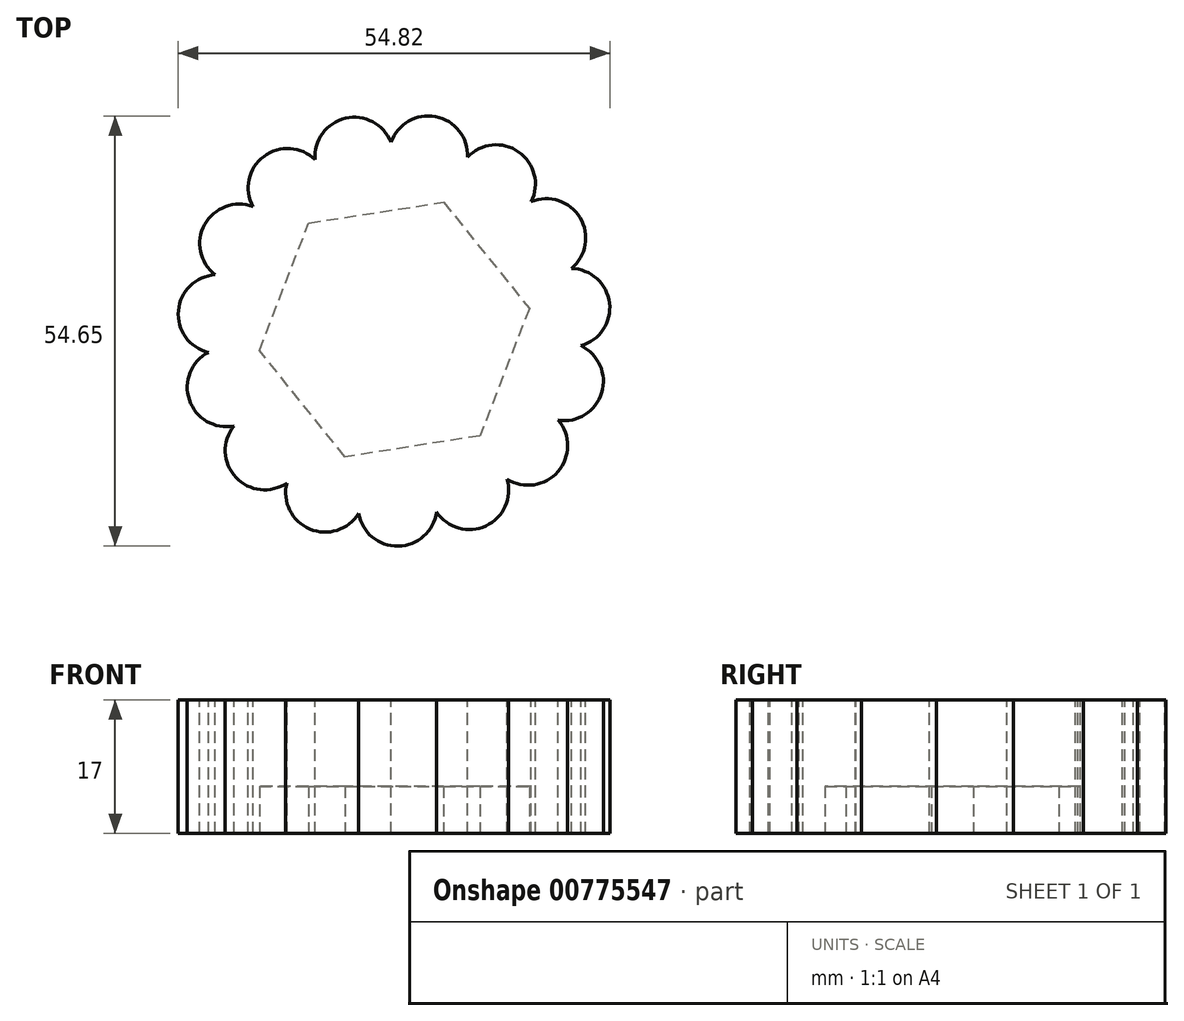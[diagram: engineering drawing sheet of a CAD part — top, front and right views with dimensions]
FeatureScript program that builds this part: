
annotation { "Feature Type Name" : "Feature", "Feature Type Description" : "" }
export const myFeature = defineFeature(function(context is Context, id is Id, definition is map)
    precondition{}
    {
        {
            var Q0;
            Q0=qCreatedBy(makeId("Top.planeOp"),FACE);
            var sketch = newSketch(context, id + "F0", { "sketchPlane" : qUnion([Q0])});
            skCircle(sketch, "E0.cCircle", {"center": v(0, 0) * mm, "radius": 17.35 * mm, "construction": true});
            skLineSegment(sketch, "E0.0", {"start": v(10.88, -13.52) * mm, "end": v(-6.27, -16.18) * mm});
            skLineSegment(sketch, "E0.1", {"start": v(-6.27, -16.18) * mm, "end": v(-17.14, -2.66) * mm});
            skLineSegment(sketch, "E0.2", {"start": v(-17.14, -2.66) * mm, "end": v(-10.88, 13.52) * mm});
            skLineSegment(sketch, "E0.3", {"start": v(-10.88, 13.52) * mm, "end": v(6.27, 16.18) * mm});
            skLineSegment(sketch, "E0.4", {"start": v(6.27, 16.18) * mm, "end": v(17.14, 2.66) * mm});
            skLineSegment(sketch, "E0.5", {"start": v(17.14, 2.66) * mm, "end": v(10.88, -13.52) * mm});
            skCircle(sketch, "E1.cCircle", {"center": v(0, 0) * mm, "radius": 22.54 * mm, "construction": true});
            skLineSegment(sketch, "E1.0", {"start": v(15.15, -16.68) * mm, "end": v(-6.87, -21.46) * mm});
            skLineSegment(sketch, "E1.1", {"start": v(-6.87, -21.46) * mm, "end": v(-22.02, -4.78) * mm});
            skLineSegment(sketch, "E1.2", {"start": v(-22.02, -4.78) * mm, "end": v(-15.15, 16.68) * mm});
            skLineSegment(sketch, "E1.3", {"start": v(-15.15, 16.68) * mm, "end": v(6.87, 21.46) * mm});
            skLineSegment(sketch, "E1.4", {"start": v(6.87, 21.46) * mm, "end": v(22.02, 4.78) * mm});
            skLineSegment(sketch, "E1.5", {"start": v(22.02, 4.78) * mm, "end": v(15.15, -16.68) * mm});
            skSolve(sketch);
        }
        {
            var Q0;
            Q0 = qSketchRegion(id + "F0", true);
            extrude(context, id + "F1", {"entities" : qUnion([Q0]), "depth" : 12 * mm, "offsetDistance" : 25 * mm});
        }
        {
            var Q0;
            Q0=makeQuery(id+"F1.opExtrude","CAP_FACE",FACE,{"disambiguationData":[OSD([sQuery(id+"F0.wireOp",EDGE,"E0.0"),sQuery(id+"F0.wireOp",EDGE,"E0.1"),sQuery(id+"F0.wireOp",EDGE,"E0.2"),sQuery(id+"F0.wireOp",EDGE,"E0.3"),sQuery(id+"F0.wireOp",EDGE,"E0.4"),sQuery(id+"F0.wireOp",EDGE,"E0.5"),sQuery(id+"F0.wireOp",EDGE,"E1.0"),sQuery(id+"F0.wireOp",EDGE,"E1.1"),sQuery(id+"F0.wireOp",EDGE,"E1.2"),sQuery(id+"F0.wireOp",EDGE,"E1.3"),sQuery(id+"F0.wireOp",EDGE,"E1.4"),sQuery(id+"F0.wireOp",EDGE,"E1.5")])],"isStart":false});
            extrude(context, id + "F2", {"entities" : qUnion([Q0]), "operationType" : NewBodyOperationType.ADD, "oppositeDirection" : true, "depth" : 6 * mm, "offsetDistance" : 25 * mm});
        }
        {
            var Q0;
            Q0=makeQuery(id+"F1.opExtrude","CAP_FACE",FACE,{"disambiguationData":[OSD([sQuery(id+"F0.wireOp",EDGE,"E0.0"),sQuery(id+"F0.wireOp",EDGE,"E0.1"),sQuery(id+"F0.wireOp",EDGE,"E0.2"),sQuery(id+"F0.wireOp",EDGE,"E0.3"),sQuery(id+"F0.wireOp",EDGE,"E0.4"),sQuery(id+"F0.wireOp",EDGE,"E0.5"),sQuery(id+"F0.wireOp",EDGE,"E1.0"),sQuery(id+"F0.wireOp",EDGE,"E1.1"),sQuery(id+"F0.wireOp",EDGE,"E1.2"),sQuery(id+"F0.wireOp",EDGE,"E1.3"),sQuery(id+"F0.wireOp",EDGE,"E1.4"),sQuery(id+"F0.wireOp",EDGE,"E1.5")])],"isStart":false});
            var sketch = newSketch(context, id + "F3", { "sketchPlane" : qUnion([Q0])});
            skCircle(sketch, "E2.cCircle", {"center": v(0, 0) * mm, "radius": 22.54 * mm, "construction": true});
            skLineSegment(sketch, "E2.0", {"start": v(15.15, -16.68) * mm, "end": v(-6.87, -21.46) * mm});
            skLineSegment(sketch, "E2.1", {"start": v(-6.87, -21.46) * mm, "end": v(-22.02, -4.78) * mm});
            skLineSegment(sketch, "E2.2", {"start": v(-22.02, -4.78) * mm, "end": v(-15.15, 16.68) * mm});
            skLineSegment(sketch, "E2.3", {"start": v(-15.15, 16.68) * mm, "end": v(6.87, 21.46) * mm});
            skLineSegment(sketch, "E2.4", {"start": v(6.87, 21.46) * mm, "end": v(22.02, 4.78) * mm});
            skLineSegment(sketch, "E2.5", {"start": v(22.02, 4.78) * mm, "end": v(15.15, -16.68) * mm});
            skSolve(sketch);
        }
        {
            var Q0;
            Q0 = qSketchRegion(id + "F3", true);
            extrude(context, id + "F4", {"entities" : qUnion([Q0]), "operationType" : NewBodyOperationType.ADD, "oppositeDirection" : true, "depth" : 6 * mm, "offsetDistance" : 25 * mm});
        }
        {
            var Q0;
            Q0=makeQuery(id+"F4.boolean.opBoolean","MERGE",FACE,{"derivedFrom":[makeQuery(id+"F1.opExtrude","CAP_FACE",FACE,{"disambiguationData":[OSD([sQuery(id+"F0.wireOp",EDGE,"E0.0"),sQuery(id+"F0.wireOp",EDGE,"E0.1"),sQuery(id+"F0.wireOp",EDGE,"E0.2"),sQuery(id+"F0.wireOp",EDGE,"E0.3"),sQuery(id+"F0.wireOp",EDGE,"E0.4"),sQuery(id+"F0.wireOp",EDGE,"E0.5"),sQuery(id+"F0.wireOp",EDGE,"E1.0"),sQuery(id+"F0.wireOp",EDGE,"E1.1"),sQuery(id+"F0.wireOp",EDGE,"E1.2"),sQuery(id+"F0.wireOp",EDGE,"E1.3"),sQuery(id+"F0.wireOp",EDGE,"E1.4"),sQuery(id+"F0.wireOp",EDGE,"E1.5")])],"isStart":false}),makeQuery(id+"F4.opExtrude","CAP_FACE",FACE,{"disambiguationData":[OSD([sQuery(id+"F3.wireOp",EDGE,"E2.0"),sQuery(id+"F3.wireOp",EDGE,"E2.1"),sQuery(id+"F3.wireOp",EDGE,"E2.2"),sQuery(id+"F3.wireOp",EDGE,"E2.3"),sQuery(id+"F3.wireOp",EDGE,"E2.4"),sQuery(id+"F3.wireOp",EDGE,"E2.5")])],"isStart":true})]});
            var sketch = newSketch(context, id + "F5", { "sketchPlane" : qUnion([Q0])});
            skCircle(sketch, "E3", {"center": v(0, 0) * mm, "radius": 22.54 * mm});
            skSolve(sketch);
        }
        {
            var Q0;
            Q0 = qSketchRegion(id + "F5", true);
            extrude(context, id + "F6", {"entities" : qUnion([Q0]), "operationType" : NewBodyOperationType.ADD, "depth" : 5 * mm, "offsetDistance" : 25 * mm});
        }
        {
            var Q0;
            Q0=makeQuery(id+"F6.opExtrude","CAP_FACE",FACE,{"disambiguationData":[OSD([sQuery(id+"F5.wireOp",EDGE,"E3")])],"isStart":false});
            var sketch = newSketch(context, id + "F7", { "sketchPlane" : qUnion([Q0])});
            skCircle(sketch, "E4", {"center": v(-13.57, 18) * mm, "radius": 5 * mm});
            skCircle(sketch, "E5.1.0", {"center": v(-19.71, 10.92) * mm, "radius": 5 * mm});
            skCircle(sketch, "E5.2.0", {"center": v(-22.45, 1.96) * mm, "radius": 5 * mm});
            skCircle(sketch, "E5.3.0", {"center": v(-21.3, -7.34) * mm, "radius": 5 * mm});
            skCircle(sketch, "E5.4.0", {"center": v(-16.48, -15.37) * mm, "radius": 5 * mm});
            skCircle(sketch, "E5.5.0", {"center": v(-8.8, -20.75) * mm, "radius": 5 * mm});
            skCircle(sketch, "E5.6.0", {"center": v(0.4, -22.53) * mm, "radius": 5 * mm});
            skCircle(sketch, "E5.7.0", {"center": v(9.53, -20.42) * mm, "radius": 5 * mm});
            skCircle(sketch, "E5.8.0", {"center": v(17.01, -14.78) * mm, "radius": 5 * mm});
            skCircle(sketch, "E5.9.0", {"center": v(21.55, -6.58) * mm, "radius": 5 * mm});
            skCircle(sketch, "E5.10.0", {"center": v(22.37, 2.75) * mm, "radius": 5 * mm});
            skCircle(sketch, "E5.11.0", {"center": v(19.31, 11.61) * mm, "radius": 5 * mm});
            skCircle(sketch, "E5.12.0", {"center": v(12.92, 18.46) * mm, "radius": 5 * mm});
            skPoint(sketch, "E5.center", {"position": v(0, 0) * mm});
            skCircle(sketch, "E6.1.13.0", {"center": v(4.3, 22.12) * mm, "radius": 5 * mm});
            skCircle(sketch, "E6.1.14.0", {"center": v(-5.08, 21.96) * mm, "radius": 5 * mm});
            skSolve(sketch);
        }
        {
            var Q0;
            Q0 = qSketchRegion(id + "F7", true);
            var Q1;
            {var subQ0=sQuery(id+"F5.wireOp",EDGE,"E3");var subQ1=makeQuery(id+"F6.opExtrude","CAP_FACE",FACE,{"disambiguationData":[OSD([subQ0])],"isStart":true});Q1=makeQuery(id+"F6.boolean.opBoolean","SPLIT",FACE,{"disambiguationData":[TD([makeQuery(id+"F1.opExtrude","SWEPT_FACE",FACE,{"disambiguationData":[OSD([sQuery(id+"F0.wireOp",EDGE,"E1.2")])]}),makeQuery(id+"F1.opExtrude","SWEPT_FACE",FACE,{"disambiguationData":[OSD([sQuery(id+"F0.wireOp",EDGE,"E1.3")])]}),makeQuery(id+"F1.opExtrude","SWEPT_FACE",FACE,{"disambiguationData":[OSD([sQuery(id+"F0.wireOp",EDGE,"E1.4")])]}),makeQuery(id+"F6.opExtrude","SWEPT_FACE",FACE,{"disambiguationData":[OSD([subQ0])]}),subQ1])],"derivedFrom":subQ1});}
            extrude(context, id + "F8", {"entities" : qUnion([Q0]), "operationType" : NewBodyOperationType.ADD, "endBound" : BoundingType.UP_TO_SURFACE, "oppositeDirection" : true, "depth" : 25 * mm, "endBoundEntityFace" : qUnion([Q1]), "offsetDistance" : 25 * mm});
        }
        {
            var Q0;
            {var subQ0=sQuery(id+"F5.wireOp",EDGE,"E3");var subQ1=makeQuery(id+"F6.opExtrude","SWEPT_FACE",FACE,{"disambiguationData":[OSD([subQ0])]});var subQ2=makeQuery(id+"F1.opExtrude","SWEPT_FACE",FACE,{"disambiguationData":[OSD([sQuery(id+"F0.wireOp",EDGE,"E1.4")])]});var subQ3=makeQuery(id+"F6.opExtrude","CAP_FACE",FACE,{"disambiguationData":[OSD([subQ0])],"isStart":true});var subQ4=makeQuery(id+"F1.opExtrude","SWEPT_FACE",FACE,{"disambiguationData":[OSD([sQuery(id+"F0.wireOp",EDGE,"E1.5")])]});var subQ5=makeQuery(id+"F1.opExtrude","SWEPT_FACE",FACE,{"disambiguationData":[OSD([sQuery(id+"F0.wireOp",EDGE,"E1.0")])]});var subQ6=makeQuery(id+"F1.opExtrude","SWEPT_FACE",FACE,{"disambiguationData":[OSD([sQuery(id+"F0.wireOp",EDGE,"E1.3")])]});var subQ7=makeQuery(id+"F1.opExtrude","SWEPT_FACE",FACE,{"disambiguationData":[OSD([sQuery(id+"F0.wireOp",EDGE,"E1.2")])]});var subQ8=makeQuery(id+"F1.opExtrude","SWEPT_FACE",FACE,{"disambiguationData":[OSD([sQuery(id+"F0.wireOp",EDGE,"E1.1")])]});Q0=makeQuery(id+"F8.boolean.opBoolean","MERGE",FACE,{"derivedFrom":[makeQuery(id+"F6.boolean.opBoolean","SPLIT",FACE,{"disambiguationData":[TD([subQ5,subQ8,subQ4,subQ1,subQ3])],"derivedFrom":subQ3}),makeQuery(id+"F6.boolean.opBoolean","SPLIT",FACE,{"disambiguationData":[TD([subQ5,subQ8,subQ7,subQ1,subQ3])],"derivedFrom":subQ3}),makeQuery(id+"F6.boolean.opBoolean","SPLIT",FACE,{"disambiguationData":[TD([subQ8,subQ7,subQ6,subQ1,subQ3])],"derivedFrom":subQ3}),makeQuery(id+"F6.boolean.opBoolean","SPLIT",FACE,{"disambiguationData":[TD([subQ7,subQ6,subQ2,subQ1,subQ3])],"derivedFrom":subQ3}),makeQuery(id+"F6.boolean.opBoolean","SPLIT",FACE,{"disambiguationData":[TD([subQ6,subQ2,subQ4,subQ1,subQ3])],"derivedFrom":subQ3}),makeQuery(id+"F6.boolean.opBoolean","SPLIT",FACE,{"disambiguationData":[TD([subQ5,subQ2,subQ4,subQ1,subQ3])],"derivedFrom":subQ3}),makeQuery(id+"F8.opExtrude","CAP_FACE",FACE,{"disambiguationData":[OSD([sQuery(id+"F7.wireOp",EDGE,"E4"),sQuery(id+"F7.wireOp",EDGE,"E5.1.0"),sQuery(id+"F7.wireOp",EDGE,"E5.2.0"),sQuery(id+"F7.wireOp",EDGE,"E5.3.0"),sQuery(id+"F7.wireOp",EDGE,"E5.4.0"),sQuery(id+"F7.wireOp",EDGE,"E5.5.0"),sQuery(id+"F7.wireOp",EDGE,"E5.6.0"),sQuery(id+"F7.wireOp",EDGE,"E5.7.0"),sQuery(id+"F7.wireOp",EDGE,"E5.8.0"),sQuery(id+"F7.wireOp",EDGE,"E5.9.0"),sQuery(id+"F7.wireOp",EDGE,"E5.10.0"),sQuery(id+"F7.wireOp",EDGE,"E5.11.0"),sQuery(id+"F7.wireOp",EDGE,"E5.12.0"),sQuery(id+"F7.wireOp",EDGE,"E6.1.13.0"),sQuery(id+"F7.wireOp",EDGE,"E6.1.14.0")])],"isStart":false})]});}
            var Q1;
            Q1=makeQuery(id+"F1.opExtrude","CAP_FACE",FACE,{"disambiguationData":[OSD([sQuery(id+"F0.wireOp",EDGE,"E0.0"),sQuery(id+"F0.wireOp",EDGE,"E0.1"),sQuery(id+"F0.wireOp",EDGE,"E0.2"),sQuery(id+"F0.wireOp",EDGE,"E0.3"),sQuery(id+"F0.wireOp",EDGE,"E0.4"),sQuery(id+"F0.wireOp",EDGE,"E0.5"),sQuery(id+"F0.wireOp",EDGE,"E1.0"),sQuery(id+"F0.wireOp",EDGE,"E1.1"),sQuery(id+"F0.wireOp",EDGE,"E1.2"),sQuery(id+"F0.wireOp",EDGE,"E1.3"),sQuery(id+"F0.wireOp",EDGE,"E1.4"),sQuery(id+"F0.wireOp",EDGE,"E1.5")])],"isStart":true});
            extrude(context, id + "F9", {"entities" : qUnion([Q0]), "operationType" : NewBodyOperationType.ADD, "endBound" : BoundingType.UP_TO_SURFACE, "depth" : 25 * mm, "endBoundEntityFace" : qUnion([Q1]), "offsetDistance" : 25 * mm});
        }
    });
